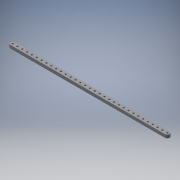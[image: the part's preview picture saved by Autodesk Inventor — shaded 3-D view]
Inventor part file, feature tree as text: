
AUTODESK INVENTOR PART (.ipt)
format: ipt  version: 2016 (Build 200138000, 138)  size: 151,040 bytes
history: native  units: in
note: dims shown in document units (in); Inventor stores cm internally (conversion verified against a paired STEP export)
features: fillet x1, other x1
ambient origin geometry x8: Origin, YZ Plane, XZ Plane, XY Plane, X Axis, Y Axis, Z Axis, Center Point
bodies: Solid1 (feature_tree)
feature tree (2):
  fillet  "Fillet1"  Radius=0.0in
  other  "LPattern1"
